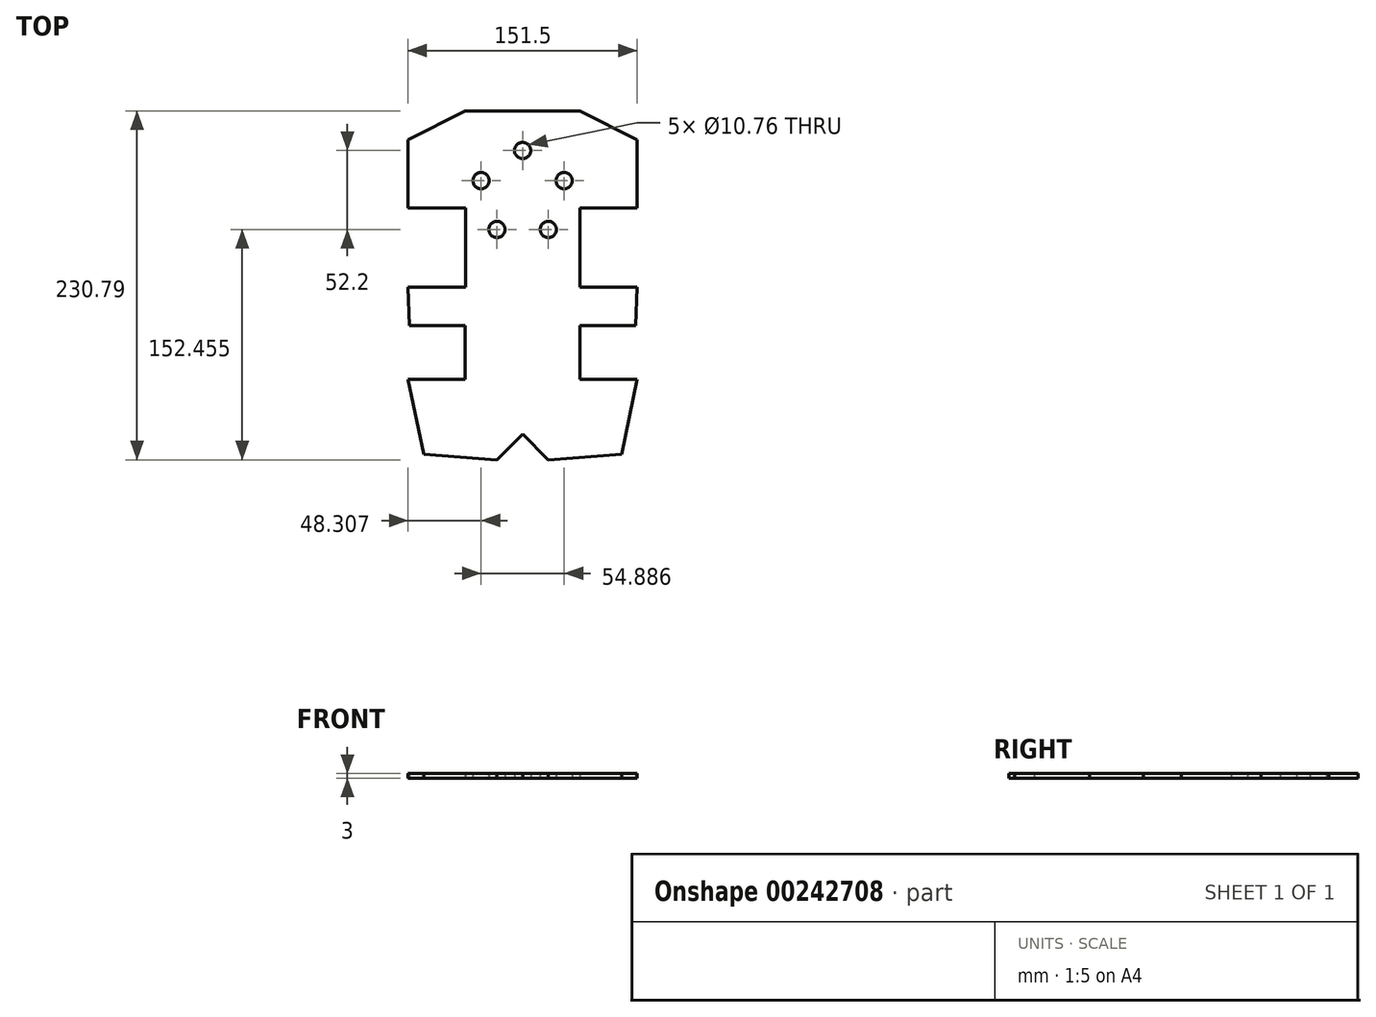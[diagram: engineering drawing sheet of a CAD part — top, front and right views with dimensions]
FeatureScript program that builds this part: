
annotation { "Feature Type Name" : "Feature", "Feature Type Description" : "" }
export const myFeature = defineFeature(function(context is Context, id is Id, definition is map)
    precondition{}
    {
        {
            var Q0;
            Q0=qCreatedBy(makeId("Top.planeOp"),FACE);
            var sketch = newSketch(context, id + "F0", { "sketchPlane" : qUnion([Q0])});
            skLineSegment(sketch, "E0", {"start": v(-37.88, 158) * mm, "end": v(-75.75, 138.8) * mm});
            skLineSegment(sketch, "E1", {"start": v(-75.75, 138.8) * mm, "end": v(-75.75, 93.92) * mm});
            skLineSegment(sketch, "E2", {"start": v(-75.75, 93.92) * mm, "end": v(-37.82, 93.92) * mm});
            skLineSegment(sketch, "E3", {"start": v(-37.82, 93.92) * mm, "end": v(-37.82, 41.33) * mm});
            skLineSegment(sketch, "E4", {"start": v(-37.82, 41.33) * mm, "end": v(-75.75, 41.33) * mm});
            skLineSegment(sketch, "E5", {"start": v(-75.75, 41.33) * mm, "end": v(-74.76, 16.06) * mm});
            skLineSegment(sketch, "E6", {"start": v(-74.76, 16.06) * mm, "end": v(-37.98, 16.06) * mm});
            skLineSegment(sketch, "E7", {"start": v(-37.98, 16.06) * mm, "end": v(-37.98, -19.4) * mm});
            skLineSegment(sketch, "E8", {"start": v(-37.98, -19.4) * mm, "end": v(-75.75, -19.4) * mm});
            skLineSegment(sketch, "E9", {"start": v(-75.75, -19.4) * mm, "end": v(-65.44, -68.88) * mm});
            skLineSegment(sketch, "E10", {"start": v(-65.44, -68.88) * mm, "end": v(-17, -72.8) * mm});
            skLineSegment(sketch, "E11", {"start": v(-17, -72.8) * mm, "end": v(0, -55.8) * mm});
            skLineSegment(sketch, "E12.MirrorCS", {"start": v(17, -72.8) * mm, "end": v(0, -55.8) * mm});
            skLineSegment(sketch, "E13.MirrorCS", {"start": v(37.88, 158) * mm, "end": v(75.75, 138.8) * mm});
            skLineSegment(sketch, "E14.MirrorCS", {"start": v(75.75, 138.8) * mm, "end": v(75.75, 93.92) * mm});
            skLineSegment(sketch, "E15.MirrorCS", {"start": v(75.75, 93.92) * mm, "end": v(37.82, 93.92) * mm});
            skLineSegment(sketch, "E16.MirrorCS", {"start": v(37.82, 93.92) * mm, "end": v(37.82, 41.33) * mm});
            skLineSegment(sketch, "E17.MirrorCS", {"start": v(37.82, 41.33) * mm, "end": v(75.75, 41.33) * mm});
            skLineSegment(sketch, "E18.MirrorCS", {"start": v(75.75, 41.33) * mm, "end": v(74.76, 16.06) * mm});
            skLineSegment(sketch, "E19.MirrorCS", {"start": v(74.76, 16.06) * mm, "end": v(37.98, 16.06) * mm});
            skLineSegment(sketch, "E20.MirrorCS", {"start": v(37.98, 16.06) * mm, "end": v(37.98, -19.4) * mm});
            skLineSegment(sketch, "E21.MirrorCS", {"start": v(37.98, -19.4) * mm, "end": v(75.75, -19.4) * mm});
            skLineSegment(sketch, "E22.MirrorCS", {"start": v(75.75, -19.4) * mm, "end": v(65.44, -68.88) * mm});
            skLineSegment(sketch, "E23.MirrorCS", {"start": v(65.44, -68.88) * mm, "end": v(17, -72.8) * mm});
            skLineSegment(sketch, "E24", {"start": v(-37.88, 158) * mm, "end": v(37.88, 158) * mm});
            skCircle(sketch, "E25", {"center": v(0, 131.86) * mm, "radius": 5.38 * mm});
            skCircle(sketch, "E26.1.0", {"center": v(-27.44, 111.92) * mm, "radius": 5.38 * mm});
            skCircle(sketch, "E26.2.0", {"center": v(-16.96, 79.66) * mm, "radius": 5.38 * mm});
            skCircle(sketch, "E26.3.0", {"center": v(16.96, 79.66) * mm, "radius": 5.38 * mm});
            skCircle(sketch, "E26.4.0", {"center": v(27.44, 111.92) * mm, "radius": 5.38 * mm});
            skPoint(sketch, "E26.center", {"position": v(0, 103) * mm});
            skSolve(sketch);
        }
        {
            var Q0;
            Q0 = qSketchRegion(id + "F0", true);
            extrude(context, id + "F1", {"entities" : qUnion([Q0]), "depth" : 3 * mm});
        }
    });
